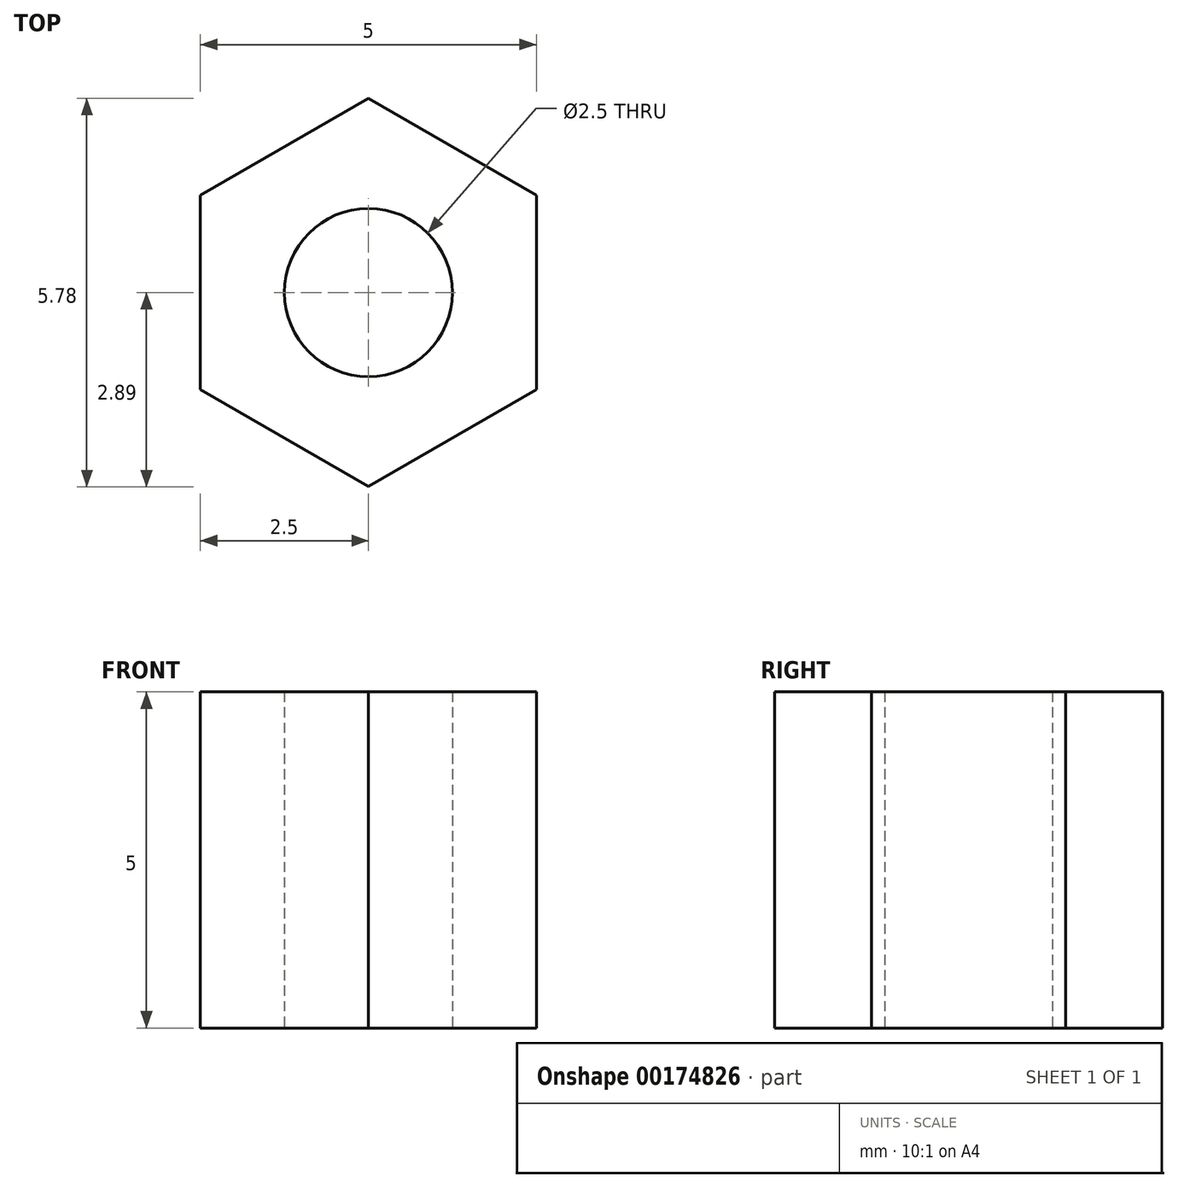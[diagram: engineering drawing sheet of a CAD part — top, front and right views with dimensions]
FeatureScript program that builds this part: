
annotation { "Feature Type Name" : "Feature", "Feature Type Description" : "" }
export const myFeature = defineFeature(function(context is Context, id is Id, definition is map)
    precondition{}
    {
        {
            var Q0;
            Q0=qCreatedBy(makeId("Top.planeOp"),FACE);
            var sketch = newSketch(context, id + "F0", { "sketchPlane" : qUnion([Q0])});
            skCircle(sketch, "E0.cCircle", {"center": v(0, 0) * mm, "radius": 2.5 * mm, "construction": true});
            skLineSegment(sketch, "E0.0", {"start": v(2.5, -1.44) * mm, "end": v(0, -2.89) * mm});
            skLineSegment(sketch, "E0.1", {"start": v(0, -2.89) * mm, "end": v(-2.5, -1.44) * mm});
            skLineSegment(sketch, "E0.2", {"start": v(-2.5, -1.44) * mm, "end": v(-2.5, 1.44) * mm});
            skLineSegment(sketch, "E0.3", {"start": v(-2.5, 1.44) * mm, "end": v(0, 2.89) * mm});
            skLineSegment(sketch, "E0.4", {"start": v(0, 2.89) * mm, "end": v(2.5, 1.44) * mm});
            skLineSegment(sketch, "E0.5", {"start": v(2.5, 1.44) * mm, "end": v(2.5, -1.44) * mm});
            skPoint(sketch, "E0.0.midPoint", {"position": v(1.25, -2.17) * mm});
            skCircle(sketch, "E1", {"center": v(0, 0) * mm, "radius": 1.25 * mm});
            skSolve(sketch);
        }
        {
            var Q0;
            Q0 = qSketchRegion(id + "F0", true);
            extrude(context, id + "F1", {"entities" : qUnion([Q0]), "depth" : 5 * mm});
        }
    });
